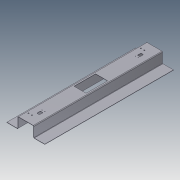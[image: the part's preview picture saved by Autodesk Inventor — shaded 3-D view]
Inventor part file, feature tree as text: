
AUTODESK INVENTOR PART (.ipt)
format: ipt  version: 2012 (Build 160160000, 160)  size: 178,688 bytes
history: native  units: in
note: dims shown in document units (in); Inventor stores cm internally (conversion verified against a paired STEP export)
features: extrude x3, pattern_linear x3, sketch x3, hole x2, plane x1, mirror x1
ambient origin geometry x8: Origin, YZ Plane, XZ Plane, XY Plane, X Axis, Y Axis, Z Axis, Center Point
bodies: Solid1 (feature_tree)
feature tree (13):
  extrude  "Extrusion1"  Depth=0.1196in
  hole  "Hole1"  [1 undecoded]
  pattern_linear  "Rectangular Pattern1"  Spacing1=0.2446in  [1 undecoded]
  pattern_linear  "Rectangular Pattern2"  Spacing1=47.5in  [1 undecoded]
  extrude  "Extrusion2"  Depth=0.7874in
  extrude  "Extrusion3"  Depth=0.3937in TaperAngle=0.0deg
  hole  "Hole2"  [1 undecoded]
  pattern_linear  "Rectangular Pattern3"  Spacing1=0.1196in  [1 undecoded]
  plane  "Work Plane1"
  mirror  "Mirror1"
  sketch  "Sketch1"  dims[d0=4.0in d1=0.1196in]
  sketch  "Sketch3"  dims[d2=0.1196in d3=6.0in]
  sketch  "Sketch4"  dims[d4=0.125in d5=0.2446in d6=47.5in d7=0.0in d13=3.0in d14=1.0in d15=0.39in d16=0.75in d17=0.375in d18=0.25in d19=0.5635in d20=1.0in d21=0.8108in d22=0.7874in d24=1.25in d25=0.3937in d27=0.0in d28=0.7874in d30=41.5in d31=0.1196in d32=0.1196in d33=0.125in d34=0.2446in d35=4.0in d36=0.25in d37=8.0in d38=4.5in d39=0.75in d40=20.0in d41=1.0in d42=0.0in d43=4.5in d44=2.2554in d45=1.0in d46=5.5108in d47=1.375in d48=0.25in d49=1.0in d50=0.0in d51=3.5in d52=0.625in d53=0.19in d54=0.75in d55=0.375in d56=0.25in d57=0.5635in d58=1.0in d59=0.8108in d60=0.7874in d62=1.0in]
note: 5 required parameter values undecoded (feature->parameter linkage not recoverable at this tier; creation-order binding heuristic only, values carry confidence <= 0.55)
